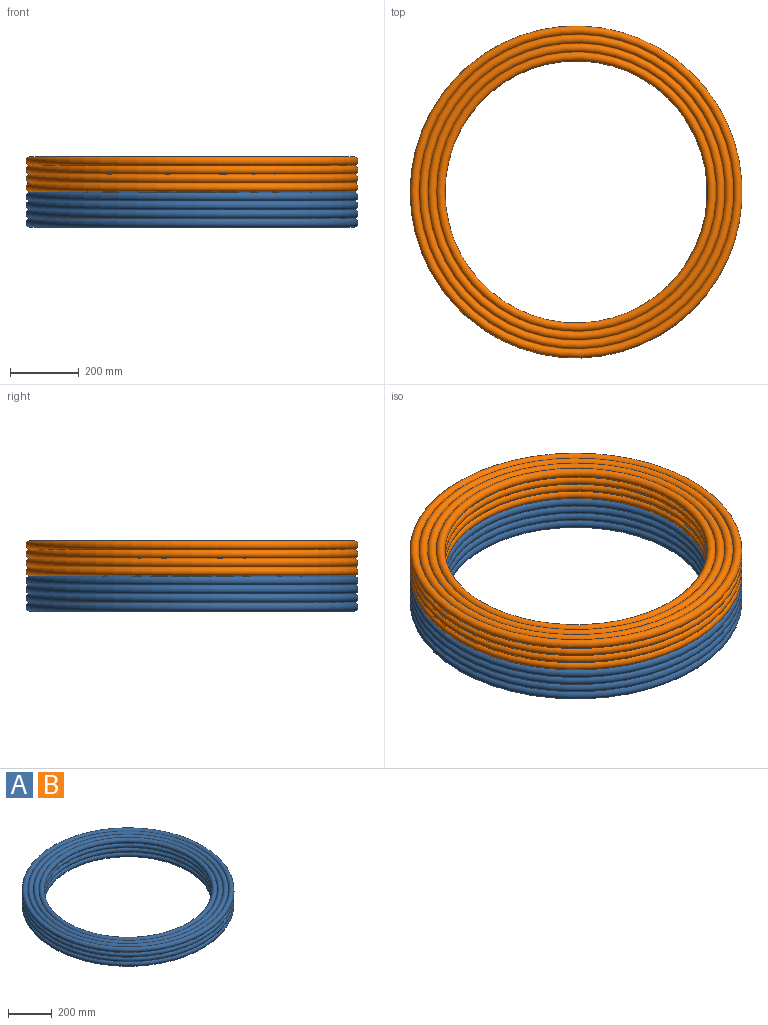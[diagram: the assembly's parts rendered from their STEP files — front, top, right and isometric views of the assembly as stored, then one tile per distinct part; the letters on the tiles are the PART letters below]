
ASSEMBLY  parts=2 mates=1
PART A: 12 faces, bbox 1044.7x1044.7x101.6 mm
  f0: torus R=419.1mm, axis (0,0,-1), area 105063.3mm2, adj f1,f11
  f1: torus R=393.7mm, axis (0,0,-1), area 147030.4mm2, adj f0,f2
  f2: torus R=393.7mm, axis (0,0,-1), area 96669mm2, adj f1,f3
  f3: torus R=393.7mm, axis (0,0,-1), area 96669mm2, adj f2,f4
  f4: torus R=393.7mm, axis (0,0,-1), area 147030.4mm2, adj f3,f5
  f5: torus R=419.1mm, axis (0,0,-1), area 105063.3mm2, adj f4,f6
  f6: torus R=444.5mm, axis (0,0,-1), area 111430.8mm2, adj f5,f7
  f7: torus R=469.9mm, axis (0,0,-1), area 177710.8mm2, adj f6,f8
  f8: torus R=469.9mm, axis (0,0,-1), area 119825.1mm2, adj f7,f9
  f9: torus R=469.9mm, axis (0,0,-1), area 119825.1mm2, adj f8,f10
  f10: torus R=469.9mm, axis (0,0,-1), area 177710.8mm2, adj f9,f11
  f11: torus R=444.5mm, axis (0,0,-1), area 111430.8mm2, adj f0,f10
PART B: same geometry as A
PLACE A at identity fixed
PLACE B t=(0,0,103.05)mm
MATE fastened B.f0 <-> A.f0  axis (0,0,-1) through (0,0,106.77)mm
